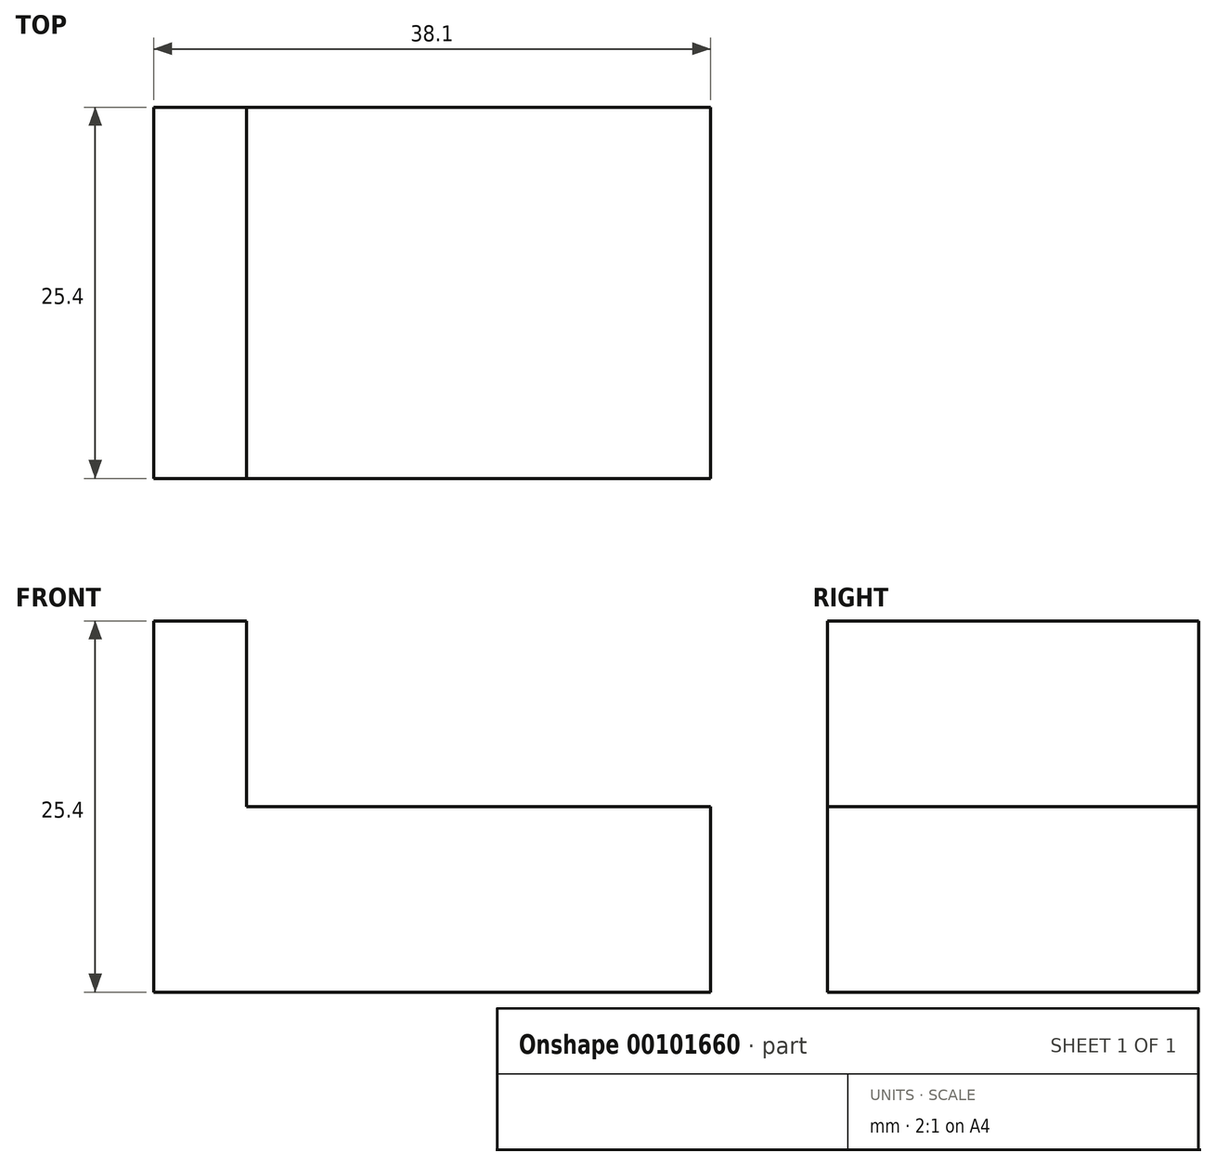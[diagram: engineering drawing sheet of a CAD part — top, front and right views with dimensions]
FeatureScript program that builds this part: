
annotation { "Feature Type Name" : "Feature", "Feature Type Description" : "" }
export const myFeature = defineFeature(function(context is Context, id is Id, definition is map)
    precondition{}
    {
        {
            var Q0;
            Q0=qCreatedBy(makeId("Front.planeOp"),FACE);
            var sketch = newSketch(context, id + "F0", { "sketchPlane" : qUnion([Q0])});
            skLineSegment(sketch, "E0", {"start": v(0, 0) * mm, "end": v(0, 25.4) * mm});
            skLineSegment(sketch, "E1", {"start": v(0, 25.4) * mm, "end": v(6.35, 25.4) * mm});
            skLineSegment(sketch, "E2", {"start": v(6.35, 25.4) * mm, "end": v(6.35, 12.7) * mm});
            skLineSegment(sketch, "E3", {"start": v(0, 0) * mm, "end": v(38.1, 0) * mm});
            skLineSegment(sketch, "E4", {"start": v(38.1, 12.7) * mm, "end": v(6.35, 12.7) * mm});
            skLineSegment(sketch, "E5", {"start": v(38.1, 0) * mm, "end": v(38.1, 12.7) * mm});
            skSolve(sketch);
        }
        {
            var Q0;
            Q0=makeQuery(id+"F0.imprint","IMPRINT",FACE,{"disambiguationData":[TD([[makeQuery(id+"F0.imprint","IMPRINT",EDGE,{"derivedFrom":sQuery(id+"F0.wireOp",EDGE,"E0")}),-1.0]])]});
            extrude(context, id + "F1", {"entities" : qUnion([Q0]), "depth" : 25.4 * mm});
        }
    });
